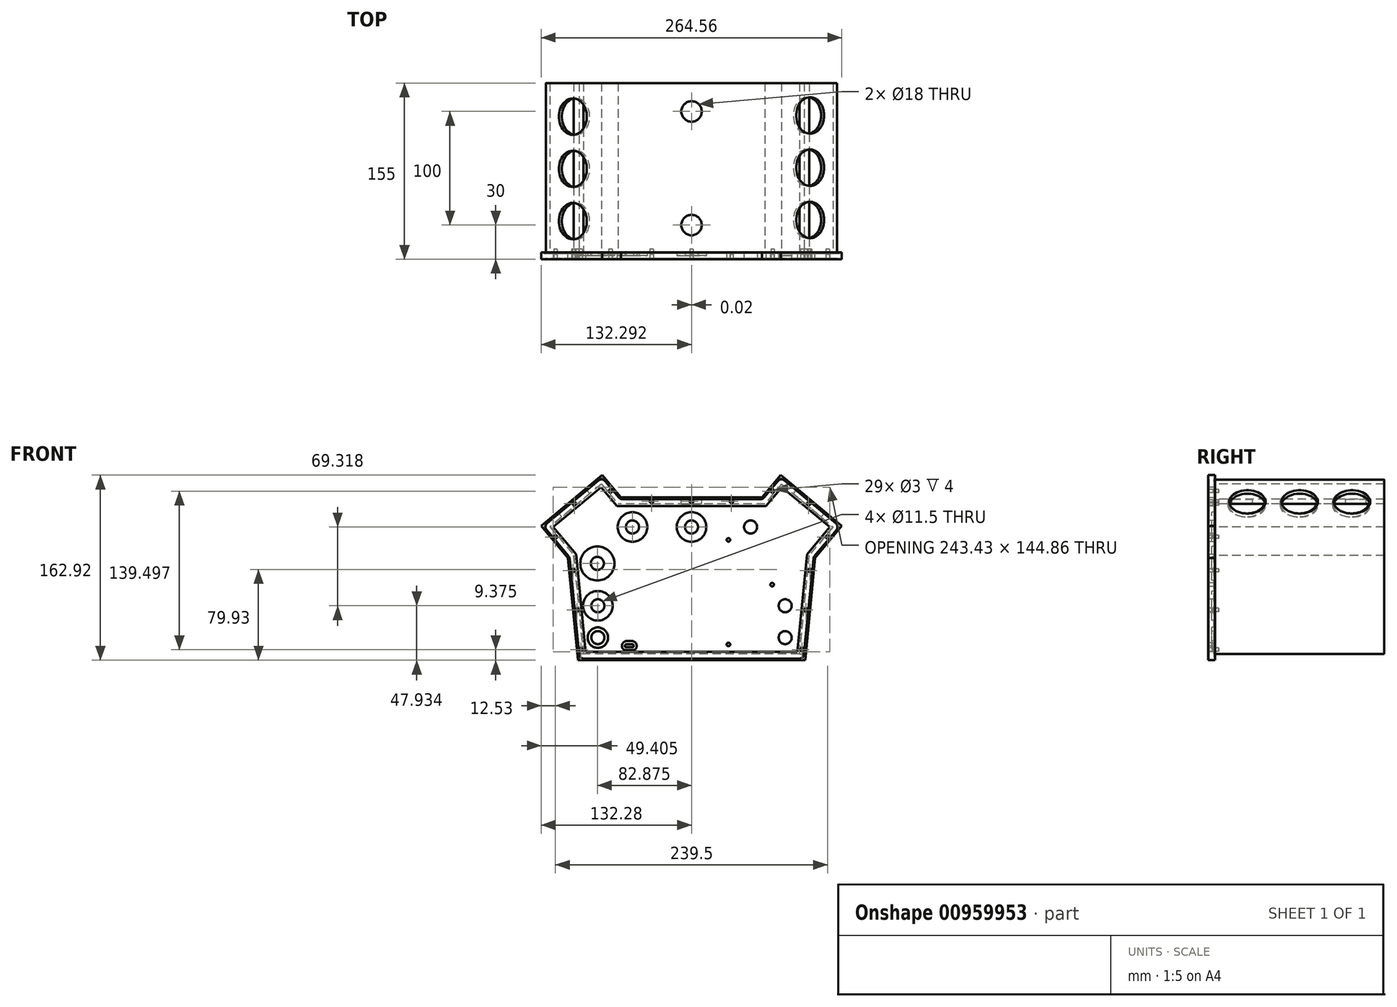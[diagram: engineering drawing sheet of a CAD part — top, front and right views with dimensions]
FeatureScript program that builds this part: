
annotation { "Feature Type Name" : "Feature", "Feature Type Description" : "" }
export const myFeature = defineFeature(function(context is Context, id is Id, definition is map)
    precondition{}
    {
        {
            var Q0;
            Q0=qCreatedBy(makeId("Front.planeOp"),FACE);
            var sketch = newSketch(context, id + "F0", { "sketchPlane" : qUnion([Q0])});
            skPoint(sketch, "E0.middle", {"position": v(0, 0) * mm});
            skLineSegment(sketch, "E1.MirrorCS", {"start": v(-108.85, 58.58) * mm, "end": v(-100, -31.42) * mm});
            skLineSegment(sketch, "E2.MirrorCS", {"start": v(-132.28, 86.7) * mm, "end": v(-108.85, 58.58) * mm});
            skLineSegment(sketch, "E3.MirrorCS", {"start": v(-78.5, 131.5) * mm, "end": v(-132.28, 86.7) * mm});
            skLineSegment(sketch, "E4", {"start": v(-78.5, 131.5) * mm, "end": v(-62.1, 111.83) * mm});
            skLineSegment(sketch, "E5", {"start": v(-62.1, 111.83) * mm, "end": v(0, 111.83) * mm});
            skLineSegment(sketch, "E6", {"start": v(-100, -31.42) * mm, "end": v(0, -31.42) * mm});
            skLineSegment(sketch, "E7.MirrorCS", {"start": v(62.1, 111.83) * mm, "end": v(0, 111.83) * mm});
            skLineSegment(sketch, "E8.MirrorCS", {"start": v(78.5, 131.5) * mm, "end": v(62.1, 111.83) * mm});
            skLineSegment(sketch, "E9.MirrorCS", {"start": v(78.5, 131.5) * mm, "end": v(132.28, 86.7) * mm});
            skLineSegment(sketch, "E10.MirrorCS", {"start": v(132.28, 86.7) * mm, "end": v(108.85, 58.58) * mm});
            skLineSegment(sketch, "E11.MirrorCS", {"start": v(108.85, 58.58) * mm, "end": v(100, -31.42) * mm});
            skLineSegment(sketch, "E12.MirrorCS", {"start": v(100, -31.42) * mm, "end": v(0, -31.42) * mm});
            skSolve(sketch);
        }
        {
            var Q0;
            Q0 = qSketchRegion(id + "F0", true);
            extrude(context, id + "F1", {"entities" : qUnion([Q0]), "depth" : 6 * mm, "offsetDistance" : 25 * mm});
        }
        {
            var Q0;
            Q0=makeQuery(id+"F1.opExtrude","CAP_FACE",FACE,{"disambiguationData":[OSD([sQuery(id+"F0.wireOp",EDGE,"E1.MirrorCS"),sQuery(id+"F0.wireOp",EDGE,"E2.MirrorCS"),sQuery(id+"F0.wireOp",EDGE,"E3.MirrorCS"),sQuery(id+"F0.wireOp",EDGE,"E4"),sQuery(id+"F0.wireOp",EDGE,"E5"),sQuery(id+"F0.wireOp",EDGE,"E6"),sQuery(id+"F0.wireOp",EDGE,"E7.MirrorCS"),sQuery(id+"F0.wireOp",EDGE,"E8.MirrorCS"),sQuery(id+"F0.wireOp",EDGE,"E9.MirrorCS"),sQuery(id+"F0.wireOp",EDGE,"E10.MirrorCS"),sQuery(id+"F0.wireOp",EDGE,"E11.MirrorCS"),sQuery(id+"F0.wireOp",EDGE,"E12.MirrorCS")])],"isStart":false});
            var sketch = newSketch(context, id + "F2", { "sketchPlane" : qUnion([Q0])});
            skLineSegment(sketch, "E13.0", {"start": v(-78.5, 131.5) * mm, "end": v(-132.28, 86.7) * mm});
            skLineSegment(sketch, "E14.0", {"start": v(-78.5, 131.5) * mm, "end": v(-62.1, 111.83) * mm});
            skLineSegment(sketch, "E15.0", {"start": v(62.1, 111.83) * mm, "end": v(-62.1, 111.83) * mm});
            skLineSegment(sketch, "E16.0", {"start": v(78.5, 131.5) * mm, "end": v(62.1, 111.83) * mm});
            skLineSegment(sketch, "E17.0", {"start": v(78.5, 131.5) * mm, "end": v(132.28, 86.7) * mm});
            skLineSegment(sketch, "E18.0", {"start": v(132.28, 86.7) * mm, "end": v(108.85, 58.58) * mm});
            skLineSegment(sketch, "E19.0", {"start": v(108.85, 58.58) * mm, "end": v(100, -31.42) * mm});
            skLineSegment(sketch, "E20.0", {"start": v(100, -31.42) * mm, "end": v(-100, -31.42) * mm});
            skLineSegment(sketch, "E21.0", {"start": v(-108.85, 58.58) * mm, "end": v(-100, -31.42) * mm});
            skLineSegment(sketch, "E22.0", {"start": v(-132.28, 86.7) * mm, "end": v(-108.85, 58.58) * mm});
            skLineSegment(sketch, "E23.0", {"start": v(-78.69, 129.4) * mm, "end": v(-62.81, 110.33) * mm});
            skLineSegment(sketch, "E23.1", {"start": v(62.81, 110.33) * mm, "end": v(-62.81, 110.33) * mm});
            skLineSegment(sketch, "E23.2", {"start": v(-78.69, 129.4) * mm, "end": v(-130.17, 86.5) * mm});
            skLineSegment(sketch, "E23.3", {"start": v(78.69, 129.4) * mm, "end": v(62.81, 110.33) * mm});
            skLineSegment(sketch, "E23.4", {"start": v(78.69, 129.4) * mm, "end": v(130.17, 86.5) * mm});
            skLineSegment(sketch, "E23.5", {"start": v(130.17, 86.5) * mm, "end": v(107.4, 59.19) * mm});
            skLineSegment(sketch, "E23.6", {"start": v(-130.17, 86.5) * mm, "end": v(-107.4, 59.19) * mm});
            skLineSegment(sketch, "E23.7", {"start": v(-107.4, 59.19) * mm, "end": v(-98.64, -29.92) * mm});
            skLineSegment(sketch, "E23.8", {"start": v(98.64, -29.92) * mm, "end": v(-98.64, -29.92) * mm});
            skLineSegment(sketch, "E23.9", {"start": v(107.4, 59.19) * mm, "end": v(98.64, -29.92) * mm});
            skLineSegment(sketch, "E24.0", {"start": v(-79.46, 120.94) * mm, "end": v(-65.62, 104.33) * mm});
            skLineSegment(sketch, "E24.1", {"start": v(65.62, 104.33) * mm, "end": v(-65.62, 104.33) * mm});
            skLineSegment(sketch, "E24.2", {"start": v(-79.46, 120.94) * mm, "end": v(-121.71, 85.74) * mm});
            skLineSegment(sketch, "E24.3", {"start": v(79.46, 120.94) * mm, "end": v(65.62, 104.33) * mm});
            skLineSegment(sketch, "E24.4", {"start": v(79.46, 120.94) * mm, "end": v(121.71, 85.74) * mm});
            skLineSegment(sketch, "E24.5", {"start": v(121.71, 85.74) * mm, "end": v(101.61, 61.6) * mm});
            skLineSegment(sketch, "E24.6", {"start": v(-121.71, 85.74) * mm, "end": v(-101.61, 61.6) * mm});
            skLineSegment(sketch, "E24.7", {"start": v(-101.61, 61.6) * mm, "end": v(-93.2, -23.92) * mm});
            skLineSegment(sketch, "E24.8", {"start": v(93.2, -23.92) * mm, "end": v(-93.2, -23.92) * mm});
            skLineSegment(sketch, "E24.9", {"start": v(101.61, 61.6) * mm, "end": v(93.2, -23.92) * mm});
            skSolve(sketch);
        }
        {
            var Q0;
            Q0=makeQuery(id+"F2.imprint","IMPRINT",FACE,{"disambiguationData":[TD([[makeQuery(id+"F2.imprint","IMPRINT",EDGE,{"derivedFrom":sQuery(id+"F2.wireOp",EDGE,"E23.0")}),-1.0]])]});
            extrude(context, id + "F3", {"entities" : qUnion([Q0]), "operationType" : NewBodyOperationType.REMOVE, "oppositeDirection" : true, "depth" : 0.5 * mm, "offsetDistance" : 25 * mm});
        }
        {
            var Q0;
            Q0=makeQuery(id+"F3.boolean.opBoolean","SPLIT",FACE,{"disambiguationData":[TD([makeQuery(id+"F3.opExtrude","SWEPT_FACE",FACE,{"disambiguationData":[OSD([sQuery(id+"F2.wireOp",EDGE,"E24.0")])]})])],"derivedFrom":makeQuery(id+"F1.opExtrude","CAP_FACE",FACE,{"disambiguationData":[OSD([sQuery(id+"F0.wireOp",EDGE,"E1.MirrorCS"),sQuery(id+"F0.wireOp",EDGE,"E2.MirrorCS"),sQuery(id+"F0.wireOp",EDGE,"E3.MirrorCS"),sQuery(id+"F0.wireOp",EDGE,"E4"),sQuery(id+"F0.wireOp",EDGE,"E5"),sQuery(id+"F0.wireOp",EDGE,"E6"),sQuery(id+"F0.wireOp",EDGE,"E7.MirrorCS"),sQuery(id+"F0.wireOp",EDGE,"E8.MirrorCS"),sQuery(id+"F0.wireOp",EDGE,"E9.MirrorCS"),sQuery(id+"F0.wireOp",EDGE,"E10.MirrorCS"),sQuery(id+"F0.wireOp",EDGE,"E11.MirrorCS"),sQuery(id+"F0.wireOp",EDGE,"E12.MirrorCS")])],"isStart":false})});
            var sketch = newSketch(context, id + "F4", { "sketchPlane" : qUnion([Q0])});
            skLineSegment(sketch, "E25", {"start": v(0, -11.47) * mm, "end": v(65, -11.47) * mm});
            skLineSegment(sketch, "E26", {"start": v(65, -11.47) * mm, "end": v(65, 68.53) * mm});
            skLineSegment(sketch, "E27", {"start": v(65, 68.53) * mm, "end": v(-65, 68.53) * mm});
            skLineSegment(sketch, "E28", {"start": v(-65, 68.53) * mm, "end": v(-65, -11.47) * mm});
            skLineSegment(sketch, "E29", {"start": v(-65, -11.47) * mm, "end": v(0, -11.47) * mm});
            skLineSegment(sketch, "E30", {"start": v(-45.03, 68.53) * mm, "end": v(-45.03, 72.53) * mm});
            skLineSegment(sketch, "E31", {"start": v(-45.03, 72.53) * mm, "end": v(-56.37, 72.53) * mm});
            skSolve(sketch);
        }
        {
            var Q0;
            Q0=makeQuery(id+"F4.imprint","IMPRINT",FACE,{"disambiguationData":[TD([[makeQuery(id+"F4.imprint","IMPRINT",EDGE,{"derivedFrom":sQuery(id+"F4.wireOp",EDGE,"E25")}),1.0]])]});
            extrude(context, id + "F5", {"entities" : qUnion([Q0]), "operationType" : NewBodyOperationType.REMOVE, "oppositeDirection" : true, "depth" : 25 * mm, "offsetDistance" : 25 * mm});
        }
        {
            var Q0;
            Q0=makeQuery(id+"F3.boolean.opBoolean","SPLIT",FACE,{"disambiguationData":[TD([makeQuery(id+"F3.opExtrude","SWEPT_FACE",FACE,{"disambiguationData":[OSD([sQuery(id+"F2.wireOp",EDGE,"E24.0")])]})])],"derivedFrom":makeQuery(id+"F1.opExtrude","CAP_FACE",FACE,{"disambiguationData":[OSD([sQuery(id+"F0.wireOp",EDGE,"E1.MirrorCS"),sQuery(id+"F0.wireOp",EDGE,"E2.MirrorCS"),sQuery(id+"F0.wireOp",EDGE,"E3.MirrorCS"),sQuery(id+"F0.wireOp",EDGE,"E4"),sQuery(id+"F0.wireOp",EDGE,"E5"),sQuery(id+"F0.wireOp",EDGE,"E6"),sQuery(id+"F0.wireOp",EDGE,"E7.MirrorCS"),sQuery(id+"F0.wireOp",EDGE,"E8.MirrorCS"),sQuery(id+"F0.wireOp",EDGE,"E9.MirrorCS"),sQuery(id+"F0.wireOp",EDGE,"E10.MirrorCS"),sQuery(id+"F0.wireOp",EDGE,"E11.MirrorCS"),sQuery(id+"F0.wireOp",EDGE,"E12.MirrorCS")])],"isStart":false})});
            var sketch = newSketch(context, id + "F6", { "sketchPlane" : qUnion([Q0])});
            skPoint(sketch, "E32.0.midPoint", {"position": v(-85.55, -23.92) * mm});
            skCircle(sketch, "E33", {"center": v(-82.45, -11.49) * mm, "radius": 5.75 * mm});
            skCircle(sketch, "E34.MirrorC", {"center": v(82.45, -11.49) * mm, "radius": 5.75 * mm});
            skLineSegment(sketch, "E35", {"start": v(-82.45, -11.49) * mm, "end": v(-82.45, 16.51) * mm, "construction": true});
            skCircle(sketch, "E36", {"center": v(-82.45, 16.51) * mm, "radius": 13 * mm});
            skPoint(sketch, "E37.endSnap0", {"position": v(85.55, -25.92) * mm});
            skCircle(sketch, "E38", {"center": v(-82.45, 16.51) * mm, "radius": 5.75 * mm});
            skCircle(sketch, "E39.MirrorC", {"center": v(82.45, 16.51) * mm, "radius": 13 * mm});
            skCircle(sketch, "E40.MirrorC", {"center": v(82.45, 16.51) * mm, "radius": 5.75 * mm});
            skCircle(sketch, "E41", {"center": v(0, 85.83) * mm, "radius": 13 * mm});
            skCircle(sketch, "E42", {"center": v(0, 85.83) * mm, "radius": 5.75 * mm});
            skCircle(sketch, "E43", {"center": v(-52, 85.83) * mm, "radius": 13 * mm});
            skLineSegment(sketch, "E44", {"start": v(-65, 68.53) * mm, "end": v(-65, 107.05) * mm, "construction": true});
            skLineSegment(sketch, "E45", {"start": v(-65, 107.05) * mm, "end": v(-63.77, 107.05) * mm, "construction": true});
            skLineSegment(sketch, "E46", {"start": v(0, 85.83) * mm, "end": v(-91.63, 85.83) * mm, "construction": true});
            skLineSegment(sketch, "E47", {"start": v(-91.63, 85.83) * mm, "end": v(-91.63, 87.1) * mm, "construction": true});
            skCircle(sketch, "E48.MirrorC", {"center": v(52, 85.83) * mm, "radius": 13 * mm});
            skCircle(sketch, "E49", {"center": v(-52, 85.83) * mm, "radius": 5.75 * mm});
            skCircle(sketch, "E50.MirrorC", {"center": v(52, 85.83) * mm, "radius": 5.75 * mm});
            skCircle(sketch, "E51", {"center": v(-82.87, 53.77) * mm, "radius": 15 * mm});
            skCircle(sketch, "E52", {"center": v(-82.87, 53.77) * mm, "radius": 5.75 * mm});
            skCircle(sketch, "E53", {"center": v(82.45, -11.49) * mm, "radius": 9 * mm});
            skCircle(sketch, "E54", {"center": v(-82.45, -11.49) * mm, "radius": 9 * mm});
            skFitSpline(sketch, "E55.0", {"points": [v(-57.69, -17.4) * mm, v(-57.9, -17.63) * mm, v(-58.13, -17.85) * mm, v(-58.36, -18.07) * mm]});
            skArc(sketch, "E56.0", {"start": v(-58.36, -18.07) * mm, "mid": v(-58.45, -18.22) * mm, "end": v(-58.49, -18.4) * mm});
            skFitSpline(sketch, "E57.0", {"points": [v(-58.49, -18.4) * mm, v(-58.49, -18.5) * mm, v(-58.49, -18.62) * mm, v(-58.49, -18.73) * mm]});
            skArc(sketch, "E58.0", {"start": v(-58.49, -19.27) * mm, "mid": v(-58.36, -19.59) * mm, "end": v(-58.04, -19.72) * mm});
            skArc(sketch, "E59.0", {"start": v(-51.44, -19.72) * mm, "mid": v(-51.12, -19.59) * mm, "end": v(-50.99, -19.27) * mm});
            skArc(sketch, "E60.0", {"start": v(-51.12, -18.07) * mm, "mid": v(-51.02, -18.22) * mm, "end": v(-50.99, -18.4) * mm});
            skFitSpline(sketch, "E61.0", {"points": [v(-51.79, -17.4) * mm, v(-51.57, -17.63) * mm, v(-51.34, -17.85) * mm, v(-51.12, -18.07) * mm]});
            skArc(sketch, "E62.0", {"start": v(-51.79, -17.4) * mm, "mid": v(-51.93, -17.3) * mm, "end": v(-52.1, -17.27) * mm});
            skArc(sketch, "E63.0", {"start": v(-57.37, -17.27) * mm, "mid": v(-57.54, -17.3) * mm, "end": v(-57.69, -17.4) * mm});
            skLineSegment(sketch, "E64", {"start": v(-58.04, -19.72) * mm, "end": v(-51.44, -19.72) * mm});
            skLineSegment(sketch, "E65", {"start": v(-58.49, -18.73) * mm, "end": v(-58.49, -19.27) * mm});
            skLineSegment(sketch, "E66", {"start": v(-57.37, -17.27) * mm, "end": v(-52.1, -17.27) * mm});
            skLineSegment(sketch, "E67", {"start": v(-50.99, -18.4) * mm, "end": v(-50.99, -19.27) * mm});
            skArc(sketch, "E68.0", {"start": v(-61.19, -19.27) * mm, "mid": v(-60.26, -21.5) * mm, "end": v(-58.04, -22.42) * mm});
            skLineSegment(sketch, "E68.1", {"start": v(-61.19, -18.73) * mm, "end": v(-61.19, -19.27) * mm});
            skFitSpline(sketch, "E68.2", {"points": [v(-49.88, -15.5) * mm, v(-49.66, -15.72) * mm, v(-49.43, -15.94) * mm, v(-49.2, -16.16) * mm]});
            skArc(sketch, "E68.3", {"start": v(-49.2, -16.16) * mm, "mid": v(-48.53, -17.19) * mm, "end": v(-48.29, -18.4) * mm});
            skLineSegment(sketch, "E68.4", {"start": v(-48.29, -18.4) * mm, "end": v(-48.29, -19.27) * mm});
            skArc(sketch, "E68.5", {"start": v(-51.44, -22.42) * mm, "mid": v(-49.2, -21.5) * mm, "end": v(-48.29, -19.27) * mm});
            skArc(sketch, "E68.6", {"start": v(-49.88, -15.5) * mm, "mid": v(-50.9, -14.81) * mm, "end": v(-52.1, -14.57) * mm});
            skLineSegment(sketch, "E68.7", {"start": v(-57.37, -14.57) * mm, "end": v(-52.1, -14.57) * mm});
            skLineSegment(sketch, "E68.8", {"start": v(-58.04, -22.42) * mm, "end": v(-51.44, -22.42) * mm});
            skArc(sketch, "E68.9", {"start": v(-57.37, -14.57) * mm, "mid": v(-58.57, -14.81) * mm, "end": v(-59.6, -15.5) * mm});
            skFitSpline(sketch, "E68.10", {"points": [v(-59.6, -15.5) * mm, v(-59.82, -15.72) * mm, v(-60.04, -15.94) * mm, v(-60.26, -16.16) * mm]});
            skArc(sketch, "E68.11", {"start": v(-60.26, -16.16) * mm, "mid": v(-60.95, -17.19) * mm, "end": v(-61.19, -18.4) * mm});
            skFitSpline(sketch, "E68.12", {"points": [v(-61.19, -18.4) * mm, v(-61.19, -18.5) * mm, v(-61.19, -18.62) * mm, v(-61.19, -18.73) * mm]});
            skLineSegment(sketch, "E69.0", {"start": v(-65, 68.53) * mm, "end": v(-65, -11.47) * mm, "construction": true});
            skLineSegment(sketch, "E70.0", {"start": v(65, 68.53) * mm, "end": v(-65, 68.53) * mm, "construction": true});
            skLineSegment(sketch, "E71.0", {"start": v(65, -11.47) * mm, "end": v(65, 68.53) * mm, "construction": true});
            skLineSegment(sketch, "E72.0", {"start": v(-65, -11.47) * mm, "end": v(0, -11.47) * mm, "construction": true});
            skLineSegment(sketch, "E73.0", {"start": v(0, -11.47) * mm, "end": v(65, -11.47) * mm, "construction": true});
            skLineSegment(sketch, "E74", {"start": v(-82.87, 53.77) * mm, "end": v(-82.87, 35.12) * mm, "construction": true});
            skLineSegment(sketch, "E75", {"start": v(-82.87, 35.12) * mm, "end": v(-65, 35.12) * mm, "construction": true});
            skLineSegment(sketch, "E76", {"start": v(-65, 35.12) * mm, "end": v(-71, 35.12) * mm, "construction": true});
            skCircle(sketch, "E77", {"center": v(-71, 35.12) * mm, "radius": 1.55 * mm});
            skLineSegment(sketch, "E78", {"start": v(-65, 68.53) * mm, "end": v(-32.5, 68.53) * mm});
            skLineSegment(sketch, "E79", {"start": v(-65, 68.53) * mm, "end": v(-32.5, 68.53) * mm, "construction": true});
            skLineSegment(sketch, "E80", {"start": v(-32.5, 68.53) * mm, "end": v(-32.5, 74.53) * mm, "construction": true});
            skLineSegment(sketch, "E81", {"start": v(-65, -11.47) * mm, "end": v(-32.5, -11.47) * mm, "construction": true});
            skLineSegment(sketch, "E82", {"start": v(-32.5, -11.47) * mm, "end": v(-32.5, -17.47) * mm, "construction": true});
            skCircle(sketch, "E83", {"center": v(-32.5, -17.47) * mm, "radius": 1.55 * mm});
            skCircle(sketch, "E84", {"center": v(-32.5, 74.53) * mm, "radius": 1.55 * mm});
            skCircle(sketch, "E85.MirrorC", {"center": v(71, 35.12) * mm, "radius": 1.55 * mm});
            skCircle(sketch, "E86.MirrorC", {"center": v(32.5, 74.53) * mm, "radius": 1.55 * mm});
            skCircle(sketch, "E87.MirrorC", {"center": v(32.5, -17.47) * mm, "radius": 1.55 * mm});
            skSolve(sketch);
        }
        {
            var Q0;
            Q0=makeQuery(id+"FM5VNNq83pcB29d_1.boolean.opBoolean","MERGE",FACE,{"derivedFrom":[makeQuery(id+"F3.boolean.opBoolean","COPY",FACE,{"derivedFrom":makeQuery(id+"F3.opExtrude","CAP_FACE",FACE,{"disambiguationData":[OSD([sQuery(id+"F2.wireOp",EDGE,"E23.0"),sQuery(id+"F2.wireOp",EDGE,"E23.1"),sQuery(id+"F2.wireOp",EDGE,"E23.2"),sQuery(id+"F2.wireOp",EDGE,"E23.3"),sQuery(id+"F2.wireOp",EDGE,"E23.4"),sQuery(id+"F2.wireOp",EDGE,"E23.5"),sQuery(id+"F2.wireOp",EDGE,"E23.6"),sQuery(id+"F2.wireOp",EDGE,"E23.7"),sQuery(id+"F2.wireOp",EDGE,"E23.8"),sQuery(id+"F2.wireOp",EDGE,"E23.9"),sQuery(id+"F2.wireOp",EDGE,"E24.0"),sQuery(id+"F2.wireOp",EDGE,"E24.1"),sQuery(id+"F2.wireOp",EDGE,"E24.2"),sQuery(id+"F2.wireOp",EDGE,"E24.3"),sQuery(id+"F2.wireOp",EDGE,"E24.4"),sQuery(id+"F2.wireOp",EDGE,"E24.5"),sQuery(id+"F2.wireOp",EDGE,"E24.6"),sQuery(id+"F2.wireOp",EDGE,"E24.7"),sQuery(id+"F2.wireOp",EDGE,"E24.8"),sQuery(id+"F2.wireOp",EDGE,"E24.9")])],"isStart":false})})],"fromTools":[makeQuery(id+"FM5VNNq83pcB29d_1.opExtrude","CAP_FACE",FACE,{"disambiguationData":[OSD([sQuery(id+"F6.wireOp",EDGE,"19bfd535-33e4-445d-bbf7-34f0983f59df.0"),sQuery(id+"F6.wireOp",EDGE,"ba388438-985e-4f98-b9a1-0ad31ee5d0f5.0"),sQuery(id+"F6.wireOp",EDGE,"7a6a3dad-e307-46a7-bebd-0d9b39b36847.0"),sQuery(id+"F6.wireOp",EDGE,"50fbfc19-8b5e-47b9-804b-897e7c6062bc.0"),sQuery(id+"F6.wireOp",EDGE,"f2aef953-ca9c-47de-a316-ef1677845491.0"),sQuery(id+"F6.wireOp",EDGE,"8ab6a69b-3acb-4a4b-a927-842cc71efe0a.0"),sQuery(id+"F6.wireOp",EDGE,"d3eb7c7d-0749-4db2-9a3b-920c206eac6b.0"),sQuery(id+"F6.wireOp",EDGE,"77568bde-cf00-4857-966c-c43c957d0918.0"),sQuery(id+"F6.wireOp",EDGE,"8362e83a-fd5f-4796-be67-a076f8bd00ec.0"),sQuery(id+"F6.wireOp",EDGE,"7c0827b7-ff6b-4fc2-87d6-0e3ea3e5fdef.0"),sQuery(id+"F6.wireOp",EDGE,"d7349c00-9019-4495-87e2-96df2db839cd.0"),sQuery(id+"F6.wireOp",EDGE,"af91e955-df92-489f-87fa-6237a25e43d9.0"),sQuery(id+"F6.wireOp",EDGE,"8f477509-0da7-4572-bcc5-eed2d40c31d2.0"),sQuery(id+"F6.wireOp",EDGE,"c48309a5-a0b4-41a5-8783-b7675c8bb7a6.0"),sQuery(id+"F6.wireOp",EDGE,"d297d669-8daf-4270-ba14-5531d257255d.0"),sQuery(id+"F6.wireOp",EDGE,"94d72ec5-448a-4801-91d7-54980a893899"),sQuery(id+"F6.wireOp",EDGE,"fc99248d-9db5-459c-bf7b-a62dc000604e"),sQuery(id+"F6.wireOp",EDGE,"64855e1c-bc74-412e-8105-856898d48c5f"),sQuery(id+"F6.wireOp",EDGE,"85de86af-d90e-4aab-bdce-d569c695d237.0"),sQuery(id+"F6.wireOp",EDGE,"85de86af-d90e-4aab-bdce-d569c695d237.1"),sQuery(id+"F6.wireOp",EDGE,"85de86af-d90e-4aab-bdce-d569c695d237.2"),sQuery(id+"F6.wireOp",EDGE,"85de86af-d90e-4aab-bdce-d569c695d237.3"),sQuery(id+"F6.wireOp",EDGE,"85de86af-d90e-4aab-bdce-d569c695d237.4"),sQuery(id+"F6.wireOp",EDGE,"85de86af-d90e-4aab-bdce-d569c695d237.5"),sQuery(id+"F6.wireOp",EDGE,"85de86af-d90e-4aab-bdce-d569c695d237.6"),sQuery(id+"F6.wireOp",EDGE,"85de86af-d90e-4aab-bdce-d569c695d237.7"),sQuery(id+"F6.wireOp",EDGE,"85de86af-d90e-4aab-bdce-d569c695d237.8"),sQuery(id+"F6.wireOp",EDGE,"85de86af-d90e-4aab-bdce-d569c695d237.9"),sQuery(id+"F6.wireOp",EDGE,"85de86af-d90e-4aab-bdce-d569c695d237.10"),sQuery(id+"F6.wireOp",EDGE,"85de86af-d90e-4aab-bdce-d569c695d237.11"),sQuery(id+"F6.wireOp",EDGE,"85de86af-d90e-4aab-bdce-d569c695d237.12"),sQuery(id+"F6.wireOp",EDGE,"85de86af-d90e-4aab-bdce-d569c695d237.13"),sQuery(id+"F6.wireOp",EDGE,"85de86af-d90e-4aab-bdce-d569c695d237.14"),sQuery(id+"F6.wireOp",EDGE,"85de86af-d90e-4aab-bdce-d569c695d237.15"),sQuery(id+"F6.wireOp",EDGE,"85de86af-d90e-4aab-bdce-d569c695d237.16"),sQuery(id+"F6.wireOp",EDGE,"85de86af-d90e-4aab-bdce-d569c695d237.17")])],"isStart":false})]});
            var sketch = newSketch(context, id + "F7", { "sketchPlane" : qUnion([Q0])});
            skLineSegment(sketch, "E88", {"start": v(105.47, 60) * mm, "end": v(96.83, -27.92) * mm, "construction": true});
            skCircle(sketch, "E89", {"center": v(100.83, 12.79) * mm, "radius": 1.5 * mm});
            skLineSegment(sketch, "E90", {"start": v(105.47, 60) * mm, "end": v(127.35, 86.25) * mm, "construction": true});
            skLineSegment(sketch, "E91", {"start": v(127.35, 86.25) * mm, "end": v(78.94, 126.57) * mm, "construction": true});
            skLineSegment(sketch, "E92", {"start": v(63.75, 108.33) * mm, "end": v(50.47, 108.33) * mm, "construction": true});
            skLineSegment(sketch, "E93", {"start": v(50.47, 108.33) * mm, "end": v(0, 108.33) * mm, "construction": true});
            skPoint(sketch, "E93.endSnap0", {"position": v(0, 104.33) * mm});
            skLineSegment(sketch, "E94", {"start": v(78.94, 126.57) * mm, "end": v(63.75, 108.33) * mm, "construction": true});
            skCircle(sketch, "E95", {"center": v(0, 108.33) * mm, "radius": 1.5 * mm});
            skCircle(sketch, "E96", {"center": v(71.35, 117.45) * mm, "radius": 1.5 * mm});
            skCircle(sketch, "E97", {"center": v(103.15, 106.41) * mm, "radius": 1.5 * mm});
            skCircle(sketch, "E98", {"center": v(97.4, -22.05) * mm, "radius": 1.5 * mm});
            skCircle(sketch, "E99", {"center": v(104.26, 47.62) * mm, "radius": 1.5 * mm});
            skLineSegment(sketch, "E100", {"start": v(71.35, 117.45) * mm, "end": v(119.75, 77.13) * mm, "construction": true});
            skCircle(sketch, "E101", {"center": v(35.17, 108.33) * mm, "radius": 1.5 * mm});
            skLineSegment(sketch, "E102", {"start": v(78.94, 126.57) * mm, "end": v(103.15, 106.41) * mm, "construction": true});
            skCircle(sketch, "E103.MirrorC", {"center": v(-97.4, -22.05) * mm, "radius": 1.5 * mm});
            skCircle(sketch, "E104.MirrorC", {"center": v(-100.83, 12.79) * mm, "radius": 1.5 * mm});
            skCircle(sketch, "E105.MirrorC", {"center": v(-104.26, 47.62) * mm, "radius": 1.5 * mm});
            skCircle(sketch, "E106.MirrorC", {"center": v(-103.15, 106.41) * mm, "radius": 1.5 * mm});
            skCircle(sketch, "E107.MirrorC", {"center": v(-71.35, 117.45) * mm, "radius": 1.5 * mm});
            skCircle(sketch, "E108.MirrorC", {"center": v(-35.17, 108.33) * mm, "radius": 1.5 * mm});
            skCircle(sketch, "E109", {"center": v(119.75, 77.13) * mm, "radius": 1.5 * mm});
            skCircle(sketch, "E110.MirrorC", {"center": v(-119.75, 77.13) * mm, "radius": 1.5 * mm});
            skSolve(sketch);
        }
        {
            var Q0;
            Q0 = qSketchRegion(id + "F7", true);
            extrude(context, id + "F8", {"entities" : qUnion([Q0]), "operationType" : NewBodyOperationType.REMOVE, "oppositeDirection" : true, "depth" : 4 * mm, "offsetDistance" : 25 * mm});
        }
        {
            var Q0;
            Q0=makeQuery(id+"F1.opExtrude","CAP_FACE",FACE,{"disambiguationData":[OSD([sQuery(id+"F0.wireOp",EDGE,"E1.MirrorCS"),sQuery(id+"F0.wireOp",EDGE,"E2.MirrorCS"),sQuery(id+"F0.wireOp",EDGE,"E3.MirrorCS"),sQuery(id+"F0.wireOp",EDGE,"E4"),sQuery(id+"F0.wireOp",EDGE,"E5"),sQuery(id+"F0.wireOp",EDGE,"E6"),sQuery(id+"F0.wireOp",EDGE,"E7.MirrorCS"),sQuery(id+"F0.wireOp",EDGE,"E8.MirrorCS"),sQuery(id+"F0.wireOp",EDGE,"E9.MirrorCS"),sQuery(id+"F0.wireOp",EDGE,"E10.MirrorCS"),sQuery(id+"F0.wireOp",EDGE,"E11.MirrorCS"),sQuery(id+"F0.wireOp",EDGE,"E12.MirrorCS")])],"isStart":true});
            var sketch = newSketch(context, id + "F9", { "sketchPlane" : qUnion([Q0])});
            skLineSegment(sketch, "E111.0", {"start": v(-78.69, 129.4) * mm, "end": v(-62.81, 110.33) * mm});
            skLineSegment(sketch, "E112.0", {"start": v(-78.69, 129.4) * mm, "end": v(-130.17, 86.5) * mm});
            skLineSegment(sketch, "E113.0", {"start": v(-130.17, 86.5) * mm, "end": v(-107.4, 59.19) * mm});
            skLineSegment(sketch, "E114.0", {"start": v(-107.4, 59.19) * mm, "end": v(-98.64, -29.92) * mm});
            skLineSegment(sketch, "E115.0", {"start": v(-62.81, 110.33) * mm, "end": v(62.81, 110.33) * mm});
            skLineSegment(sketch, "E116.0", {"start": v(78.69, 129.4) * mm, "end": v(62.81, 110.33) * mm});
            skLineSegment(sketch, "E117.0", {"start": v(78.69, 129.4) * mm, "end": v(130.17, 86.5) * mm});
            skLineSegment(sketch, "E118.0", {"start": v(130.17, 86.5) * mm, "end": v(107.4, 59.19) * mm});
            skLineSegment(sketch, "E119.0", {"start": v(107.4, 59.19) * mm, "end": v(98.64, -29.92) * mm});
            skLineSegment(sketch, "E120.0", {"start": v(-98.64, -29.92) * mm, "end": v(98.64, -29.92) * mm});
            skLineSegment(sketch, "E121.0", {"start": v(-79.21, 123.62) * mm, "end": v(-64.73, 106.23) * mm});
            skLineSegment(sketch, "E121.1", {"start": v(-64.73, 106.23) * mm, "end": v(64.73, 106.23) * mm});
            skLineSegment(sketch, "E121.2", {"start": v(-79.21, 123.62) * mm, "end": v(-124.4, 85.98) * mm});
            skLineSegment(sketch, "E121.3", {"start": v(79.21, 123.62) * mm, "end": v(64.73, 106.23) * mm});
            skLineSegment(sketch, "E121.4", {"start": v(79.21, 123.62) * mm, "end": v(124.4, 85.98) * mm});
            skLineSegment(sketch, "E121.5", {"start": v(124.4, 85.98) * mm, "end": v(103.45, 60.84) * mm});
            skLineSegment(sketch, "E121.6", {"start": v(-124.4, 85.98) * mm, "end": v(-103.45, 60.84) * mm});
            skLineSegment(sketch, "E121.7", {"start": v(-103.45, 60.84) * mm, "end": v(-94.92, -25.82) * mm});
            skLineSegment(sketch, "E121.8", {"start": v(-94.92, -25.82) * mm, "end": v(94.92, -25.82) * mm});
            skLineSegment(sketch, "E121.9", {"start": v(103.45, 60.84) * mm, "end": v(94.92, -25.82) * mm});
            skCircle(sketch, "E122.0", {"center": v(103.15, 106.41) * mm, "radius": 1.5 * mm});
            skSolve(sketch);
        }
        {
            var Q0;
            Q0 = qSketchRegion(id + "F9", true);
            extrude(context, id + "F10", {"entities" : qUnion([Q0]), "operationType" : NewBodyOperationType.REMOVE, "oppositeDirection" : true, "depth" : 1 * mm, "offsetDistance" : 25 * mm});
        }
        {
            var Q0;
            Q0=makeQuery(id+"F10.boolean.opBoolean","COPY",EDGE,{"derivedFrom":makeQuery(id+"F10.opExtrude","CAP_EDGE",EDGE,{"disambiguationData":[OSD([sQuery(id+"F9.wireOp",EDGE,"E119.0")])],"isStart":false})});
            cPlane(context, id + "F11", {"entities" : qUnion([Q0]), "cplaneType" : CPlaneType.LINE_ANGLE, "offset" : 25 * mm, "angle" : 90 * degree, "width" : 150 * mm, "height" : 150 * mm});
        }
        {
            var Q0;
            Q0=qCreatedBy(id+"F11.planeOp",FACE);
            var sketch = newSketch(context, id + "F12", { "sketchPlane" : qUnion([Q0])});
            skLineSegment(sketch, "E123.0", {"start": v(130.17, 86.5) * mm, "end": v(107.4, 59.19) * mm});
            skLineSegment(sketch, "E124.0", {"start": v(78.69, 129.4) * mm, "end": v(130.17, 86.5) * mm});
            skLineSegment(sketch, "E125.0", {"start": v(78.69, 129.4) * mm, "end": v(62.81, 110.33) * mm});
            skLineSegment(sketch, "E126.0", {"start": v(-62.81, 110.33) * mm, "end": v(62.81, 110.33) * mm});
            skLineSegment(sketch, "E127.0", {"start": v(-78.69, 129.4) * mm, "end": v(-62.81, 110.33) * mm});
            skLineSegment(sketch, "E128.0", {"start": v(-78.69, 129.4) * mm, "end": v(-130.17, 86.5) * mm});
            skLineSegment(sketch, "E129.0", {"start": v(-130.17, 86.5) * mm, "end": v(-107.4, 59.19) * mm});
            skLineSegment(sketch, "E130.1", {"start": v(124.53, 86) * mm, "end": v(103.55, 60.8) * mm});
            skLineSegment(sketch, "E130.2", {"start": v(79.2, 123.76) * mm, "end": v(124.53, 86) * mm});
            skLineSegment(sketch, "E130.3", {"start": v(79.2, 123.76) * mm, "end": v(64.68, 106.33) * mm});
            skLineSegment(sketch, "E130.4", {"start": v(-64.68, 106.33) * mm, "end": v(64.68, 106.33) * mm});
            skLineSegment(sketch, "E130.6", {"start": v(-124.53, 86) * mm, "end": v(-103.55, 60.8) * mm});
            skLineSegment(sketch, "E130.7", {"start": v(-79.2, 123.76) * mm, "end": v(-124.53, 86) * mm});
            skLineSegment(sketch, "E130.8", {"start": v(-79.2, 123.76) * mm, "end": v(-64.68, 106.33) * mm});
            skLineSegment(sketch, "E131", {"start": v(95.01, -25.92) * mm, "end": v(99.03, -25.92) * mm});
            skLineSegment(sketch, "E132", {"start": v(95.01, -25.92) * mm, "end": v(103.55, 60.8) * mm});
            skLineSegment(sketch, "E133", {"start": v(-95.01, -25.92) * mm, "end": v(-99.03, -25.92) * mm});
            skLineSegment(sketch, "E134", {"start": v(-95.01, -25.92) * mm, "end": v(-103.55, 60.8) * mm});
            skLineSegment(sketch, "E135", {"start": v(-107.4, 59.19) * mm, "end": v(-99.03, -25.92) * mm});
            skLineSegment(sketch, "E136", {"start": v(99.03, -25.92) * mm, "end": v(107.4, 59.19) * mm});
            skSolve(sketch);
        }
        {
            var Q0;
            Q0 = qSketchRegion(id + "F12", true);
            extrude(context, id + "F13", {"entities" : qUnion([Q0]), "depth" : 150 * mm, "offsetDistance" : 25 * mm});
        }
        {
            var Q0;
            Q0=makeQuery(id+"F13.opExtrude","CAP_FACE",FACE,{"disambiguationData":[OSD([sQuery(id+"F12.wireOp",EDGE,"E123.0"),sQuery(id+"F12.wireOp",EDGE,"E124.0"),sQuery(id+"F12.wireOp",EDGE,"E125.0"),sQuery(id+"F12.wireOp",EDGE,"E126.0"),sQuery(id+"F12.wireOp",EDGE,"E127.0"),sQuery(id+"F12.wireOp",EDGE,"E128.0"),sQuery(id+"F12.wireOp",EDGE,"E129.0"),sQuery(id+"F12.wireOp",EDGE,"E130.1"),sQuery(id+"F12.wireOp",EDGE,"E130.2"),sQuery(id+"F12.wireOp",EDGE,"E130.3"),sQuery(id+"F12.wireOp",EDGE,"E130.4"),sQuery(id+"F12.wireOp",EDGE,"E130.6"),sQuery(id+"F12.wireOp",EDGE,"E130.7"),sQuery(id+"F12.wireOp",EDGE,"E130.8"),sQuery(id+"F12.wireOp",EDGE,"E131"),sQuery(id+"F12.wireOp",EDGE,"E132"),sQuery(id+"F12.wireOp",EDGE,"E133"),sQuery(id+"F12.wireOp",EDGE,"E134"),sQuery(id+"F12.wireOp",EDGE,"E135"),sQuery(id+"F12.wireOp",EDGE,"E136")])],"isStart":true});
            var sketch = newSketch(context, id + "F14", { "sketchPlane" : qUnion([Q0])});
            skCircle(sketch, "E137.0", {"center": v(71.35, 117.45) * mm, "radius": 1.5 * mm});
            skCircle(sketch, "E138.0", {"center": v(103.15, 106.41) * mm, "radius": 1.5 * mm});
            skCircle(sketch, "E139.0", {"center": v(119.75, 77.13) * mm, "radius": 1.5 * mm});
            skCircle(sketch, "E140.0", {"center": v(104.26, 47.62) * mm, "radius": 1.5 * mm});
            skCircle(sketch, "E141.0", {"center": v(100.83, 12.79) * mm, "radius": 1.5 * mm});
            skCircle(sketch, "E142.0", {"center": v(97.4, -22.05) * mm, "radius": 1.5 * mm});
            skCircle(sketch, "E143.0", {"center": v(-97.4, -22.05) * mm, "radius": 1.5 * mm});
            skCircle(sketch, "E144.0", {"center": v(-100.83, 12.79) * mm, "radius": 1.5 * mm});
            skCircle(sketch, "E145.0", {"center": v(-104.26, 47.62) * mm, "radius": 1.5 * mm});
            skCircle(sketch, "E146.0", {"center": v(-119.75, 77.13) * mm, "radius": 1.5 * mm});
            skCircle(sketch, "E147.0", {"center": v(-103.15, 106.41) * mm, "radius": 1.5 * mm});
            skCircle(sketch, "E148.0", {"center": v(-71.35, 117.45) * mm, "radius": 1.5 * mm});
            skCircle(sketch, "E149.0", {"center": v(-35.17, 108.33) * mm, "radius": 1.5 * mm});
            skCircle(sketch, "E150.0", {"center": v(0, 108.33) * mm, "radius": 1.5 * mm});
            skSolve(sketch);
        }
        {
            var Q0;
            Q0 = qSketchRegion(id + "F14", true);
            extrude(context, id + "F15", {"entities" : qUnion([Q0]), "operationType" : NewBodyOperationType.REMOVE, "oppositeDirection" : true, "depth" : 4 * mm, "offsetDistance" : 25 * mm});
        }
        {
            var Q0;
            Q0=makeQuery(id+"F6.imprint","IMPRINT",FACE,{"disambiguationData":[TD([[makeQuery(id+"F6.imprint","IMPRINT",EDGE,{"derivedFrom":sQuery(id+"F6.wireOp",EDGE,"E33")}),-1.0]])]});
            var Q1;
            Q1=makeQuery(id+"F6.imprint","IMPRINT",FACE,{"disambiguationData":[TD([[makeQuery(id+"F6.imprint","IMPRINT",EDGE,{"derivedFrom":sQuery(id+"F6.wireOp",EDGE,"E34.MirrorC")}),1.0]])]});
            var Q2;
            Q2=makeQuery(id+"F6.imprint","IMPRINT",FACE,{"disambiguationData":[TD([[makeQuery(id+"F6.imprint","IMPRINT",EDGE,{"derivedFrom":sQuery(id+"F6.wireOp",EDGE,"E36")}),1.0]])]});
            var Q3;
            Q3=makeQuery(id+"F6.imprint","IMPRINT",FACE,{"disambiguationData":[TD([[makeQuery(id+"F6.imprint","IMPRINT",EDGE,{"derivedFrom":sQuery(id+"F6.wireOp",EDGE,"E39.MirrorC")}),-1.0]])]});
            var Q4;
            Q4=makeQuery(id+"F6.imprint","IMPRINT",FACE,{"disambiguationData":[TD([[makeQuery(id+"F6.imprint","IMPRINT",EDGE,{"derivedFrom":sQuery(id+"F6.wireOp",EDGE,"E41")}),1.0]])]});
            var Q5;
            Q5=makeQuery(id+"F6.imprint","IMPRINT",FACE,{"disambiguationData":[TD([[makeQuery(id+"F6.imprint","IMPRINT",EDGE,{"derivedFrom":sQuery(id+"F6.wireOp",EDGE,"E43")}),1.0]])]});
            var Q6;
            Q6=makeQuery(id+"F6.imprint","IMPRINT",FACE,{"disambiguationData":[TD([[makeQuery(id+"F6.imprint","IMPRINT",EDGE,{"derivedFrom":sQuery(id+"F6.wireOp",EDGE,"E48.MirrorC")}),-1.0]])]});
            var Q7;
            Q7=makeQuery(id+"F6.imprint","IMPRINT",FACE,{"disambiguationData":[TD([[makeQuery(id+"F6.imprint","IMPRINT",EDGE,{"derivedFrom":sQuery(id+"F6.wireOp",EDGE,"E51")}),1.0]])]});
            var Q8;
            Q8=makeQuery(id+"F6.imprint","IMPRINT",FACE,{"disambiguationData":[TD([[makeQuery(id+"F6.imprint","IMPRINT",EDGE,{"derivedFrom":sQuery(id+"F6.wireOp",EDGE,"E55.0")}),-1.0]])]});
            extrude(context, id + "F16", {"entities" : qUnion([Q0, Q1, Q2, Q3, Q4, Q5, Q6, Q7, Q8]), "operationType" : NewBodyOperationType.REMOVE, "oppositeDirection" : true, "depth" : 3 * mm, "offsetDistance" : 25 * mm});
        }
        {
            var Q0;
            Q0=makeQuery(id+"F6.imprint","IMPRINT",FACE,{"disambiguationData":[TD([[makeQuery(id+"F6.imprint","IMPRINT",EDGE,{"derivedFrom":sQuery(id+"F6.wireOp",EDGE,"E38")}),1.0]])]});
            var Q1;
            Q1=makeQuery(id+"F6.imprint","IMPRINT",FACE,{"disambiguationData":[TD([[makeQuery(id+"F6.imprint","IMPRINT",EDGE,{"derivedFrom":sQuery(id+"F6.wireOp",EDGE,"E33")}),1.0]])]});
            var Q2;
            Q2=makeQuery(id+"F6.imprint","IMPRINT",FACE,{"disambiguationData":[TD([[makeQuery(id+"F6.imprint","IMPRINT",EDGE,{"derivedFrom":sQuery(id+"F6.wireOp",EDGE,"E40.MirrorC")}),-1.0]])]});
            var Q3;
            Q3=makeQuery(id+"F6.imprint","IMPRINT",FACE,{"disambiguationData":[TD([[makeQuery(id+"F6.imprint","IMPRINT",EDGE,{"derivedFrom":sQuery(id+"F6.wireOp",EDGE,"E34.MirrorC")}),-1.0]])]});
            var Q4;
            Q4=makeQuery(id+"F6.imprint","IMPRINT",FACE,{"disambiguationData":[TD([[makeQuery(id+"F6.imprint","IMPRINT",EDGE,{"derivedFrom":sQuery(id+"F6.wireOp",EDGE,"E52")}),1.0]])]});
            var Q5;
            Q5=makeQuery(id+"F6.imprint","IMPRINT",FACE,{"disambiguationData":[TD([[makeQuery(id+"F6.imprint","IMPRINT",EDGE,{"derivedFrom":sQuery(id+"F6.wireOp",EDGE,"E49")}),1.0]])]});
            var Q6;
            Q6=makeQuery(id+"F6.imprint","IMPRINT",FACE,{"disambiguationData":[TD([[makeQuery(id+"F6.imprint","IMPRINT",EDGE,{"derivedFrom":sQuery(id+"F6.wireOp",EDGE,"E42")}),1.0]])]});
            var Q7;
            Q7=makeQuery(id+"F6.imprint","IMPRINT",FACE,{"disambiguationData":[TD([[makeQuery(id+"F6.imprint","IMPRINT",EDGE,{"derivedFrom":sQuery(id+"F6.wireOp",EDGE,"E50.MirrorC")}),-1.0]])]});
            var Q8;
            Q8=makeQuery(id+"F6.imprint","IMPRINT",FACE,{"disambiguationData":[TD([[makeQuery(id+"F6.imprint","IMPRINT",EDGE,{"derivedFrom":sQuery(id+"F6.wireOp",EDGE,"E55.0")}),1.0]])]});
            var Q9;
            Q9=makeQuery(id+"F6.imprint","IMPRINT",FACE,{"disambiguationData":[TD([[makeQuery(id+"F6.imprint","IMPRINT",EDGE,{"derivedFrom":sQuery(id+"F6.wireOp",EDGE,"E83")}),1.0]])]});
            var Q10;
            Q10=makeQuery(id+"F6.imprint","IMPRINT",FACE,{"disambiguationData":[TD([[makeQuery(id+"F6.imprint","IMPRINT",EDGE,{"derivedFrom":sQuery(id+"F6.wireOp",EDGE,"E87.MirrorC")}),-1.0]])]});
            var Q11;
            Q11=makeQuery(id+"F6.imprint","IMPRINT",FACE,{"disambiguationData":[TD([[makeQuery(id+"F6.imprint","IMPRINT",EDGE,{"derivedFrom":sQuery(id+"F6.wireOp",EDGE,"E84")}),1.0]])]});
            var Q12;
            Q12=makeQuery(id+"F6.imprint","IMPRINT",FACE,{"disambiguationData":[TD([[makeQuery(id+"F6.imprint","IMPRINT",EDGE,{"derivedFrom":sQuery(id+"F6.wireOp",EDGE,"E86.MirrorC")}),-1.0]])]});
            var Q13;
            Q13=makeQuery(id+"F6.imprint","IMPRINT",FACE,{"disambiguationData":[TD([[makeQuery(id+"F6.imprint","IMPRINT",EDGE,{"derivedFrom":sQuery(id+"F6.wireOp",EDGE,"E77")}),1.0]])]});
            var Q14;
            Q14=makeQuery(id+"F6.imprint","IMPRINT",FACE,{"disambiguationData":[TD([[makeQuery(id+"F6.imprint","IMPRINT",EDGE,{"derivedFrom":sQuery(id+"F6.wireOp",EDGE,"E85.MirrorC")}),-1.0]])]});
            extrude(context, id + "F17", {"entities" : qUnion([Q0, Q1, Q2, Q3, Q4, Q5, Q6, Q7, Q8, Q9, Q10, Q11, Q12, Q13, Q14]), "operationType" : NewBodyOperationType.REMOVE, "oppositeDirection" : true, "depth" : 8 * mm, "offsetDistance" : 25 * mm});
        }
        {
            var Q0;
            Q0=makeQuery(id+"F13.opExtrude","SWEPT_EDGE",EDGE,{"disambiguationData":[OSD([sQuery(id+"F12.wireOp",EDGE,"E128.0"),sQuery(id+"F12.wireOp",EDGE,"E129.0")])]});
            var Q1;
            Q1=makeQuery(id+"F13.opExtrude","SWEPT_EDGE",EDGE,{"disambiguationData":[OSD([sQuery(id+"F12.wireOp",EDGE,"E127.0"),sQuery(id+"F12.wireOp",EDGE,"E128.0")])]});
            var Q2;
            Q2=makeQuery(id+"F13.opExtrude","SWEPT_EDGE",EDGE,{"disambiguationData":[OSD([sQuery(id+"F12.wireOp",EDGE,"E125.0"),sQuery(id+"F12.wireOp",EDGE,"E126.0")])]});
            var Q3;
            Q3=makeQuery(id+"F13.opExtrude","SWEPT_EDGE",EDGE,{"disambiguationData":[OSD([sQuery(id+"F12.wireOp",EDGE,"E124.0"),sQuery(id+"F12.wireOp",EDGE,"E125.0")])]});
            var Q4;
            Q4=makeQuery(id+"F13.opExtrude","SWEPT_EDGE",EDGE,{"disambiguationData":[OSD([sQuery(id+"F12.wireOp",EDGE,"E126.0"),sQuery(id+"F12.wireOp",EDGE,"E127.0")])]});
            var Q5;
            Q5=makeQuery(id+"F13.opExtrude","SWEPT_EDGE",EDGE,{"disambiguationData":[OSD([sQuery(id+"F12.wireOp",EDGE,"E123.0"),sQuery(id+"F12.wireOp",EDGE,"E124.0")])]});
            var Q6;
            Q6=makeQuery(id+"F13.opExtrude","SWEPT_EDGE",EDGE,{"disambiguationData":[OSD([sQuery(id+"F12.wireOp",EDGE,"E123.0"),sQuery(id+"F12.wireOp",EDGE,"E136")])]});
            var Q7;
            Q7=makeQuery(id+"F13.opExtrude","SWEPT_EDGE",EDGE,{"disambiguationData":[OSD([sQuery(id+"F12.wireOp",EDGE,"E129.0"),sQuery(id+"F12.wireOp",EDGE,"E135")])]});
            fillet(context, id + "F18", {"entities" : qUnion([Q0, Q1, Q2, Q3, Q4, Q5, Q6, Q7]), "radius" : 5 * mm, "tangentPropagation" : true, "allowEdgeOverflow" : false});
        }
        {
            var Q0;
            Q0=makeQuery(id+"F13.opExtrude","SWEPT_FACE",FACE,{"disambiguationData":[OSD([sQuery(id+"F12.wireOp",EDGE,"E128.0")])]});
            var sketch = newSketch(context, id + "F19", { "sketchPlane" : qUnion([Q0])});
            skLineSegment(sketch, "E151.0.0", {"start": v(39.64, 149) * mm, "end": v(-17.36, 149) * mm, "construction": true});
            skLineSegment(sketch, "E151.0.1", {"start": v(-17.36, 149) * mm, "end": v(-17.36, -1) * mm, "construction": true});
            skLineSegment(sketch, "E151.0.2", {"start": v(-17.36, -1) * mm, "end": v(39.64, -1) * mm, "construction": true});
            skLineSegment(sketch, "E151.0.3", {"start": v(39.64, -1) * mm, "end": v(39.64, 149) * mm, "construction": true});
            skLineSegment(sketch, "E152", {"start": v(-17.36, 50.55) * mm, "end": v(11.14, 50.55) * mm});
            skLineSegment(sketch, "E153", {"start": v(11.14, 0) * mm, "end": v(11.14, 28.5) * mm, "construction": true});
            skCircle(sketch, "E154", {"center": v(11.14, 28.5) * mm, "radius": 16 * mm});
            skLineSegment(sketch, "E155", {"start": v(11.14, 28.5) * mm, "end": v(11.14, 74.5) * mm, "construction": true});
            skCircle(sketch, "E156", {"center": v(11.14, 74.5) * mm, "radius": 16 * mm});
            skLineSegment(sketch, "E157", {"start": v(11.14, 74.5) * mm, "end": v(11.14, 120.5) * mm, "construction": true});
            skCircle(sketch, "E158", {"center": v(11.14, 120.5) * mm, "radius": 16 * mm});
            skSolve(sketch);
        }
        {
            var Q0;
            Q0=makeQuery(id+"F13.opExtrude","SWEPT_FACE",FACE,{"disambiguationData":[OSD([sQuery(id+"F12.wireOp",EDGE,"E124.0")])]});
            var sketch = newSketch(context, id + "F20", { "sketchPlane" : qUnion([Q0])});
            skLineSegment(sketch, "E159.0.0", {"start": v(17.36, 149) * mm, "end": v(-39.64, 149) * mm, "construction": true});
            skLineSegment(sketch, "E159.0.1", {"start": v(-39.64, 149) * mm, "end": v(-39.64, -1) * mm, "construction": true});
            skLineSegment(sketch, "E159.0.2", {"start": v(-39.64, -1) * mm, "end": v(17.36, -1) * mm, "construction": true});
            skLineSegment(sketch, "E159.0.3", {"start": v(17.36, -1) * mm, "end": v(17.36, 149) * mm, "construction": true});
            skLineSegment(sketch, "E160", {"start": v(-39.64, 43.9) * mm, "end": v(-11.14, 43.9) * mm, "construction": true});
            skLineSegment(sketch, "E161", {"start": v(-11.14, -1) * mm, "end": v(-11.14, 27.5) * mm, "construction": true});
            skCircle(sketch, "E162", {"center": v(-11.14, 27.5) * mm, "radius": 16 * mm});
            skCircle(sketch, "E163", {"center": v(-11.14, 73.5) * mm, "radius": 16 * mm});
            skCircle(sketch, "E164", {"center": v(-11.14, 119.5) * mm, "radius": 16 * mm});
            skSolve(sketch);
        }
        {
            var Q0;
            Q0=makeQuery(id+"F19.imprint","IMPRINT",FACE,{"disambiguationData":[TD([[makeQuery(id+"F19.imprint","IMPRINT",EDGE,{"derivedFrom":sQuery(id+"F19.wireOp",EDGE,"E154")}),1.0]])]});
            var Q1;
            Q1=makeQuery(id+"F19.imprint","IMPRINT",FACE,{"disambiguationData":[TD([[makeQuery(id+"F19.imprint","IMPRINT",EDGE,{"derivedFrom":sQuery(id+"F19.wireOp",EDGE,"E156")}),1.0]])]});
            var Q2;
            Q2=makeQuery(id+"F19.imprint","IMPRINT",FACE,{"disambiguationData":[TD([[makeQuery(id+"F19.imprint","IMPRINT",EDGE,{"derivedFrom":sQuery(id+"F19.wireOp",EDGE,"E158")}),1.0]])]});
            extrude(context, id + "F21", {"entities" : qUnion([Q0, Q1, Q2]), "operationType" : NewBodyOperationType.REMOVE, "oppositeDirection" : true, "depth" : 4 * mm, "offsetDistance" : 25 * mm});
        }
        {
            var Q0;
            Q0=makeQuery(id+"F20.imprint","IMPRINT",FACE,{"disambiguationData":[TD([[makeQuery(id+"F20.imprint","IMPRINT",EDGE,{"derivedFrom":sQuery(id+"F20.wireOp",EDGE,"E164")}),1.0]])]});
            var Q1;
            Q1=makeQuery(id+"F20.imprint","IMPRINT",FACE,{"disambiguationData":[TD([[makeQuery(id+"F20.imprint","IMPRINT",EDGE,{"derivedFrom":sQuery(id+"F20.wireOp",EDGE,"E163")}),1.0]])]});
            var Q2;
            Q2=makeQuery(id+"F20.imprint","IMPRINT",FACE,{"disambiguationData":[TD([[makeQuery(id+"F20.imprint","IMPRINT",EDGE,{"derivedFrom":sQuery(id+"F20.wireOp",EDGE,"E162")}),1.0]])]});
            extrude(context, id + "F22", {"entities" : qUnion([Q0, Q1, Q2]), "operationType" : NewBodyOperationType.REMOVE, "oppositeDirection" : true, "depth" : 4 * mm, "offsetDistance" : 25 * mm});
        }
        {
            var Q0;
            Q0=makeQuery(id+"F3.boolean.opBoolean","COPY",EDGE,{"derivedFrom":makeQuery(id+"F3.opExtrude","SWEPT_EDGE",EDGE,{"disambiguationData":[OSD([sQuery(id+"F2.wireOp",EDGE,"E23.0"),sQuery(id+"F2.wireOp",EDGE,"E23.2")])]})});
            var Q1;
            Q1=makeQuery(id+"F3.boolean.opBoolean","COPY",EDGE,{"derivedFrom":makeQuery(id+"F3.opExtrude","SWEPT_EDGE",EDGE,{"disambiguationData":[OSD([sQuery(id+"F2.wireOp",EDGE,"E23.0"),sQuery(id+"F2.wireOp",EDGE,"E23.1")])]})});
            var Q2;
            Q2=makeQuery(id+"F3.boolean.opBoolean","COPY",EDGE,{"derivedFrom":makeQuery(id+"F3.opExtrude","SWEPT_EDGE",EDGE,{"disambiguationData":[OSD([sQuery(id+"F2.wireOp",EDGE,"E24.0"),sQuery(id+"F2.wireOp",EDGE,"E24.1")])]})});
            var Q3;
            Q3=makeQuery(id+"F3.boolean.opBoolean","COPY",EDGE,{"derivedFrom":makeQuery(id+"F3.opExtrude","SWEPT_EDGE",EDGE,{"disambiguationData":[OSD([sQuery(id+"F2.wireOp",EDGE,"E24.0"),sQuery(id+"F2.wireOp",EDGE,"E24.2")])]})});
            var Q4;
            Q4=makeQuery(id+"F3.boolean.opBoolean","COPY",EDGE,{"derivedFrom":makeQuery(id+"F3.opExtrude","SWEPT_EDGE",EDGE,{"disambiguationData":[OSD([sQuery(id+"F2.wireOp",EDGE,"E23.2"),sQuery(id+"F2.wireOp",EDGE,"E23.6")])]})});
            var Q5;
            Q5=makeQuery(id+"F3.boolean.opBoolean","COPY",EDGE,{"derivedFrom":makeQuery(id+"F3.opExtrude","SWEPT_EDGE",EDGE,{"disambiguationData":[OSD([sQuery(id+"F2.wireOp",EDGE,"E24.2"),sQuery(id+"F2.wireOp",EDGE,"E24.6")])]})});
            var Q6;
            Q6=makeQuery(id+"F3.boolean.opBoolean","COPY",EDGE,{"derivedFrom":makeQuery(id+"F3.opExtrude","SWEPT_EDGE",EDGE,{"disambiguationData":[OSD([sQuery(id+"F2.wireOp",EDGE,"E23.6"),sQuery(id+"F2.wireOp",EDGE,"E23.7")])]})});
            var Q7;
            Q7=makeQuery(id+"F3.boolean.opBoolean","COPY",EDGE,{"derivedFrom":makeQuery(id+"F3.opExtrude","SWEPT_EDGE",EDGE,{"disambiguationData":[OSD([sQuery(id+"F2.wireOp",EDGE,"E24.6"),sQuery(id+"F2.wireOp",EDGE,"E24.7")])]})});
            var Q8;
            Q8=makeQuery(id+"F3.boolean.opBoolean","COPY",EDGE,{"derivedFrom":makeQuery(id+"F3.opExtrude","SWEPT_EDGE",EDGE,{"disambiguationData":[OSD([sQuery(id+"F2.wireOp",EDGE,"E24.1"),sQuery(id+"F2.wireOp",EDGE,"E24.3")])]})});
            var Q9;
            Q9=makeQuery(id+"F3.boolean.opBoolean","COPY",EDGE,{"derivedFrom":makeQuery(id+"F3.opExtrude","SWEPT_EDGE",EDGE,{"disambiguationData":[OSD([sQuery(id+"F2.wireOp",EDGE,"E24.3"),sQuery(id+"F2.wireOp",EDGE,"E24.4")])]})});
            var Q10;
            Q10=makeQuery(id+"F3.boolean.opBoolean","COPY",EDGE,{"derivedFrom":makeQuery(id+"F3.opExtrude","SWEPT_EDGE",EDGE,{"disambiguationData":[OSD([sQuery(id+"F2.wireOp",EDGE,"E24.4"),sQuery(id+"F2.wireOp",EDGE,"E24.5")])]})});
            var Q11;
            Q11=makeQuery(id+"F3.boolean.opBoolean","COPY",EDGE,{"derivedFrom":makeQuery(id+"F3.opExtrude","SWEPT_EDGE",EDGE,{"disambiguationData":[OSD([sQuery(id+"F2.wireOp",EDGE,"E24.5"),sQuery(id+"F2.wireOp",EDGE,"E24.9")])]})});
            var Q12;
            Q12=makeQuery(id+"F3.boolean.opBoolean","COPY",EDGE,{"derivedFrom":makeQuery(id+"F3.opExtrude","SWEPT_EDGE",EDGE,{"disambiguationData":[OSD([sQuery(id+"F2.wireOp",EDGE,"E24.8"),sQuery(id+"F2.wireOp",EDGE,"E24.9")])]})});
            var Q13;
            Q13=makeQuery(id+"F3.boolean.opBoolean","COPY",EDGE,{"derivedFrom":makeQuery(id+"F3.opExtrude","SWEPT_EDGE",EDGE,{"disambiguationData":[OSD([sQuery(id+"F2.wireOp",EDGE,"E23.8"),sQuery(id+"F2.wireOp",EDGE,"E23.9")])]})});
            var Q14;
            Q14=makeQuery(id+"F3.boolean.opBoolean","COPY",EDGE,{"derivedFrom":makeQuery(id+"F3.opExtrude","SWEPT_EDGE",EDGE,{"disambiguationData":[OSD([sQuery(id+"F2.wireOp",EDGE,"E23.5"),sQuery(id+"F2.wireOp",EDGE,"E23.9")])]})});
            var Q15;
            Q15=makeQuery(id+"F3.boolean.opBoolean","COPY",EDGE,{"derivedFrom":makeQuery(id+"F3.opExtrude","SWEPT_EDGE",EDGE,{"disambiguationData":[OSD([sQuery(id+"F2.wireOp",EDGE,"E23.4"),sQuery(id+"F2.wireOp",EDGE,"E23.5")])]})});
            var Q16;
            Q16=makeQuery(id+"F3.boolean.opBoolean","COPY",EDGE,{"derivedFrom":makeQuery(id+"F3.opExtrude","SWEPT_EDGE",EDGE,{"disambiguationData":[OSD([sQuery(id+"F2.wireOp",EDGE,"E23.3"),sQuery(id+"F2.wireOp",EDGE,"E23.4")])]})});
            var Q17;
            Q17=makeQuery(id+"F3.boolean.opBoolean","COPY",EDGE,{"derivedFrom":makeQuery(id+"F3.opExtrude","SWEPT_EDGE",EDGE,{"disambiguationData":[OSD([sQuery(id+"F2.wireOp",EDGE,"E23.1"),sQuery(id+"F2.wireOp",EDGE,"E23.3")])]})});
            var Q18;
            Q18=makeQuery(id+"F3.boolean.opBoolean","COPY",EDGE,{"derivedFrom":makeQuery(id+"F3.opExtrude","SWEPT_EDGE",EDGE,{"disambiguationData":[OSD([sQuery(id+"F2.wireOp",EDGE,"E24.7"),sQuery(id+"F2.wireOp",EDGE,"E24.8")])]})});
            var Q19;
            Q19=makeQuery(id+"F3.boolean.opBoolean","COPY",EDGE,{"derivedFrom":makeQuery(id+"F3.opExtrude","SWEPT_EDGE",EDGE,{"disambiguationData":[OSD([sQuery(id+"F2.wireOp",EDGE,"E23.7"),sQuery(id+"F2.wireOp",EDGE,"E23.8")])]})});
            fillet(context, id + "F23", {"entities" : qUnion([Q0, Q1, Q2, Q3, Q4, Q5, Q6, Q7, Q8, Q9, Q10, Q11, Q12, Q13, Q14, Q15, Q16, Q17, Q18, Q19]), "radius" : 4 * mm, "tangentPropagation" : true, "allowEdgeOverflow" : false});
        }
        {
            var Q0;
            Q0=makeQuery(id+"F13.opExtrude","SWEPT_FACE",FACE,{"disambiguationData":[OSD([sQuery(id+"F12.wireOp",EDGE,"E126.0")])]});
            var sketch = newSketch(context, id + "F24", { "sketchPlane" : qUnion([Q0])});
            skLineSegment(sketch, "E165.0", {"start": v(-60.47, 149) * mm, "end": v(-60.47, -1) * mm, "construction": true});
            skLineSegment(sketch, "E166.0", {"start": v(60.47, -1) * mm, "end": v(60.47, 149) * mm});
            skLineSegment(sketch, "E167", {"start": v(-60.47, 63.05) * mm, "end": v(0.03, 63.05) * mm, "construction": true});
            skCircle(sketch, "E168", {"center": v(0.01, 24) * mm, "radius": 9 * mm});
            skLineSegment(sketch, "E169", {"start": v(0.03, 63.05) * mm, "end": v(0.03, 143.22) * mm, "construction": true});
            skCircle(sketch, "E170", {"center": v(0.03, 124) * mm, "radius": 9 * mm});
            skLineSegment(sketch, "E171", {"start": v(0.01, 24) * mm, "end": v(0.03, 124) * mm});
            skSolve(sketch);
        }
        {
            var Q0;
            Q0=makeQuery(id+"F24.imprint","IMPRINT",FACE,{"disambiguationData":[TD([[makeQuery(id+"F24.imprint","IMPRINT",EDGE,{"derivedFrom":sQuery(id+"F24.wireOp",EDGE,"E168")}),1.0]])]});
            var Q1;
            Q1=makeQuery(id+"F24.imprint","IMPRINT",FACE,{"disambiguationData":[TD([[makeQuery(id+"F24.imprint","IMPRINT",EDGE,{"derivedFrom":sQuery(id+"F24.wireOp",EDGE,"E170")}),1.0]])]});
            extrude(context, id + "F25", {"entities" : qUnion([Q0, Q1]), "operationType" : NewBodyOperationType.REMOVE, "oppositeDirection" : true, "depth" : 25 * mm, "offsetDistance" : 25 * mm});
        }
    });
